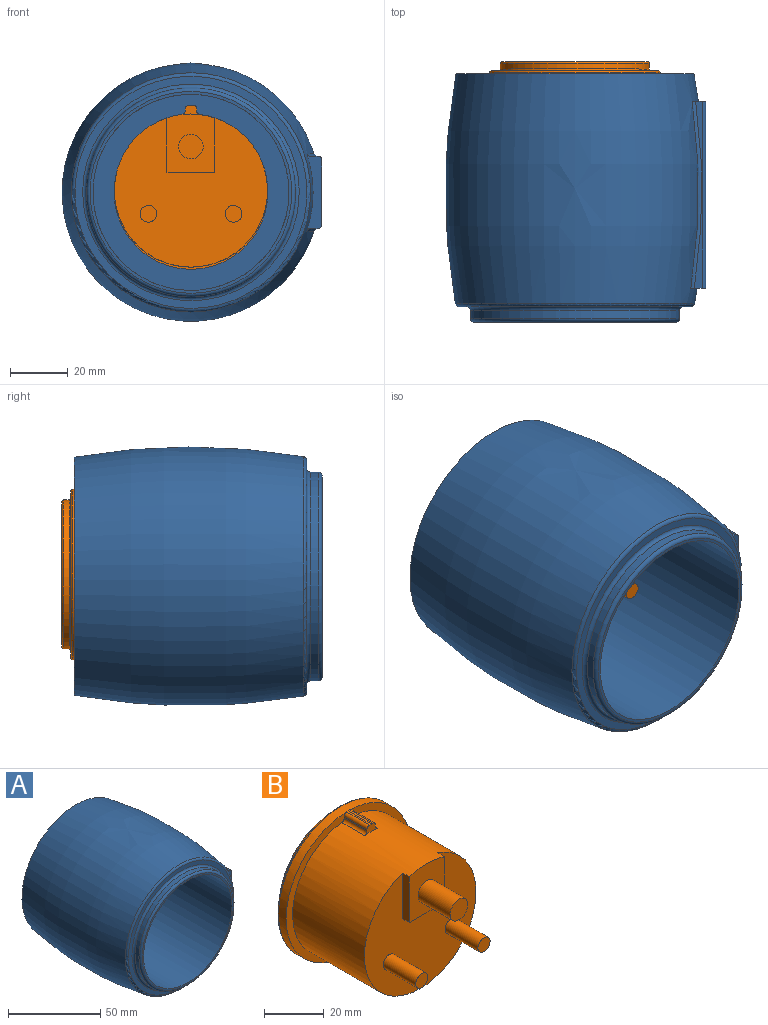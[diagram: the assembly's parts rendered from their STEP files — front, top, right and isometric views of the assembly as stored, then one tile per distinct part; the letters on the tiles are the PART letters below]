
ASSEMBLY  parts=2 mates=1
PART A: 22 faces, bbox 90x90.8x89.6 mm
  f0: revolved ~89.39x89.39mm, area 20040.4mm2, adj f5,f11,f13,f15,f16,f19
  f1: plane 69.7x69.7mm, normal (0,-1,0), area 214.3mm2, adj f9,f21
  f2: cylinder r=26.54mm len=53.09mm, axis (0,1,0), area 529.5mm2, adj f3,f8
  f3: plane 58.93x58.93mm, normal (0,1,0), area 514mm2, adj f2,f4
  f4: cone r=29.46mm half-angle=66.6deg, axis (0,1,0), area 1678.7mm2, adj f3,f5
  f5: plane 82.29x82.29mm, normal (0,1,0), area 1049.7mm2, adj f0,f4
  f6: plane 80.15x80.15mm, normal (0,-1,0), area 653.9mm2, adj f19,f20
  f7: cylinder r=36.12mm len=72.24mm, axis (0,1,0), area 637.8mm2, adj f20,f21
  f8: plane 67.71x67.71mm, normal (0,-1,0), area 1387.9mm2, adj f2,f9
  f9: cylinder r=33.86mm len=79.31mm, axis (0,-1,0), area 16872.6mm2, adj f1,f8
  f10: plane 64.54x2.73mm, normal (0,0,-1), area 57mm2, adj f11,f13,f16,f18
  f11: plane 26.77x4.78mm, normal (0,1,0), area 79.6mm2, adj f0,f10,f12,f14,f15,f16,f17,f18
  f12: plane 64.53x2.72mm, normal (0,0,1), area 57mm2, adj f11,f13,f15,f17
  f13: plane 26.77x5.25mm, normal (0,-1,0), area 90.9mm2, adj f0,f10,f12,f14,f15,f16,f17,f18
  f14: plane 64.5x22.44mm, normal (1,0,0), area 1447.1mm2, adj f11,f13,f17,f18
  f15: bspline ~88.62x5.87mm, area 103.8mm2, adj f0,f11,f12,f13
  f16: bspline ~78x5.3mm, area 103.8mm2, adj f0,f10,f11,f13
  f17: cylinder r=1.27mm len=64.5mm, axis (0,-1,0), area 128.7mm2, adj f11,f12,f13,f14
  f18: cylinder r=1.27mm len=64.5mm, axis (0,1,0), area 128.7mm2, adj f10,f11,f13,f14
  f19: torus R=40.08mm, axis (0,-1,0), area 455.8mm2, adj f0,f6
  f20: torus R=37.39mm, axis (0,-1,0), area 458.5mm2, adj f6,f7
  f21: torus R=34.85mm, axis (0,-1,0), area 447mm2, adj f1,f7
PART B: 31 faces, bbox 63.8x59.8x63.8 mm
  f0: plane 52.88x51.55mm, normal (0,-1,0), area 1819.3mm2, adj f1,f21,f22,f23,f27,f29
  f1: cylinder r=26.44mm len=52.88mm, axis (0,1,0), area 5641mm2, adj f0,f6,f16,f19,f20,f22,f23,f24
  f2: plane 50.24x50.24mm, normal (0,1,0), area 248.3mm2, adj f9,f10
  f3: cylinder r=25.76mm len=51.51mm, axis (0,-1,0), area 300.1mm2, adj f10,f11
  f4: plane 57.66x57.66mm, normal (0,1,0), area 423mm2, adj f11,f12
  f5: cylinder r=29.46mm len=58.93mm, axis (0,-1,0), area 680.4mm2, adj f6,f12,f14,f16,f17
  f6: plane 58.93x58.93mm, normal (0,-1,0), area 519mm2, adj f1,f5,f13,f14,f15,f17,f18,f19
  f7: cylinder r=22.86mm len=45.72mm, axis (0,1,0), area 182.4mm2, adj f8,f9
  f8: plane 45.72x45.72mm, normal (0,1,0), area 1641.7mm2, adj f7
  f9: torus R=23.49mm, axis (0,1,0), area 144.7mm2, adj f2,f7
  f10: torus R=25.12mm, axis (0,1,0), area 160mm2, adj f2,f3
  f11: torus R=26.39mm, axis (0,1,0), area 162.9mm2, adj f3,f4
  f12: torus R=28.83mm, axis (0,1,0), area 183.2mm2, adj f4,f5
  f13: plane 10.8x0.67mm, normal (1,0,0), area 7.2mm2, adj f6,f16,f17,f20
  f14: plane 10.8x0.75mm, normal (-0.03,0,1), area 8.1mm2, adj f5,f6,f16,f18
  f15: plane 10.8x0.65mm, normal (-1,0,0), area 7mm2, adj f6,f16,f18,f19
  f16: plane 6.2x3.21mm, normal (0,-1,0), area 11.9mm2, adj f1,f5,f13,f14,f15,f17,f18,f19
  f17: cylinder r=1.27mm len=10.8mm, axis (0,-1,0), area 21.2mm2, adj f5,f6,f13,f16
  f18: cylinder r=1.27mm len=10.8mm, axis (0,1,0), area 21.1mm2, adj f6,f14,f15,f16
  f19: cylinder r=1.27mm len=10.8mm, axis (0,1,0), area 19.9mm2, adj f1,f6,f15,f16
  f20: cylinder r=1.27mm len=10.8mm, axis (0,1,0), area 19.9mm2, adj f1,f6,f13,f16
  f21: plane 16.56x3.18mm, normal (0,0,-1), area 52.6mm2, adj f0,f22,f23,f24
  f22: plane 18.76x3.18mm, normal (1,0,0), area 59.6mm2, adj f0,f1,f21,f24
  f23: plane 18.76x3.18mm, normal (-1,0,0), area 59.6mm2, adj f0,f1,f21,f24
  f24: plane 20.09x16.56mm, normal (0,-1,0), area 269.4mm2, adj f1,f21,f22,f23,f25
  f25: cylinder r=4.22mm len=15.24mm, axis (0,1,0), area 404.6mm2, adj f24,f26
  f26: plane 8.45x8.45mm, normal (0,-1,0), area 56.1mm2, adj f25
  f27: cylinder r=2.87mm len=15.49mm, axis (0,1,0), area 279.2mm2, adj f0,f28
  f28: plane 5.74x5.74mm, normal (0,-1,0), area 25.8mm2, adj f27
  f29: cylinder r=2.87mm len=15.49mm, axis (0,1,0), area 279.2mm2, adj f0,f30
  f30: plane 5.74x5.74mm, normal (0,-1,0), area 25.8mm2, adj f29
PLACE A t=(24.17,-13.95,43.93)mm
PLACE B t=(24.17,-7.67,44.57)mm
MATE planar A.f2 <-> B.f6  axis (0,1,0) through (24.17,-7.67,43.93)mm
